# Revit family: Reece_Accessory_Kado_Lux_HiFlow_LED Inline Exhaust System_Square_Outlet Grille
name_source: partatom
category: Air Terminals
revit_build: Autodesk Revit 2018 (Build: 20180329_1100(x64)
units: mm (PartAtom-declared; Revit-internal decimal feet)

## family parameters
Cut with Voids When Loaded = Yes
Host = Face
Part Type = Normal
Room Calculation Point = Yes
Round Connector Dimension = Use Diameter
Shared = Yes

## types (2) — shared parameters
CW Connection = No
Disclaimer = THIS FILE IS THE PROPERTY OF THE REECE GROUP. IT MAY NOT BE REPRODUCED, REVERSE-ENGINEERED OR MODIFIED. ANY REPUBLICATION, TRANSMISSION OR DISTRIBUTION FOR THE PURPOSE OF COMMERCIALLY EXPLOITING THE FILES IS PROHIBITED.
HW Connection = No
Manufacturer = Kado
Max Flow = 561.0 m³/h
Min Flow = 438.0 m³/h
Model = Lux
Reece_Detail_Additional = HiFlow
Reece_Detail_Connector = Plug in (Plug & Lead included)
Reece_Detail_Installation = LED Inline Exhaust System
Reece_Detail_Note = Electrical input required. Refer to web page for further details.
Reece_Material_Main = Reece_Plastic_ABS_White
Reece_Mechanical_Duct_Diameter = 150 mm
Reece_Overall_Length = 208 mm
Reece_Overall_Width = 208 mm
Reece_Product_Brand = Kado
Reece_Product_Mount = Ceiling Mounted
Reece_Product_Sub Brand = Lux
Reece_Product_Type = Accessory
Reece_Product_Web Page = https://www.reece.com.au
Type Comments = Accessory
URL = https://www.reece.com.au
Vent Connection = No
Waste Connection = No
zero-valued in all types: Default Elevation

## per-type parameters (varying)
| type | Description | Keynote | Reece_Product_Description | Reece_Product_Number |
| 270 mm x 270 mm_Matte Black | Kado Lux HiFlow LED Inline Exhaust System Square Matte Black | Product #2020369 (3of3), Reece_Accessory_Kado_Lux_HiFlow_LED Inline Exhaust System_Square_Outlet Grille - Matte Black | Kado Lux HiFlow LED Inline Exhaust System Square Matte Black | 2020369 (3of3) |
| 270 mm x 270 mm_Matte White | Kado Lux HiFlow LED Inline Exhaust System Square Matte White | Product #2020370 (3of3), Reece_Accessory_Kado_Lux_HiFlow_LED Inline Exhaust System_Square_Outlet Grille - Matte White | Kado Lux HiFlow LED Inline Exhaust System Square Matte White | 2020370 (3of3) |

## geometry (parser evidence)
native form markers: Sweep x2
no freeform markers — native parametric forms only
